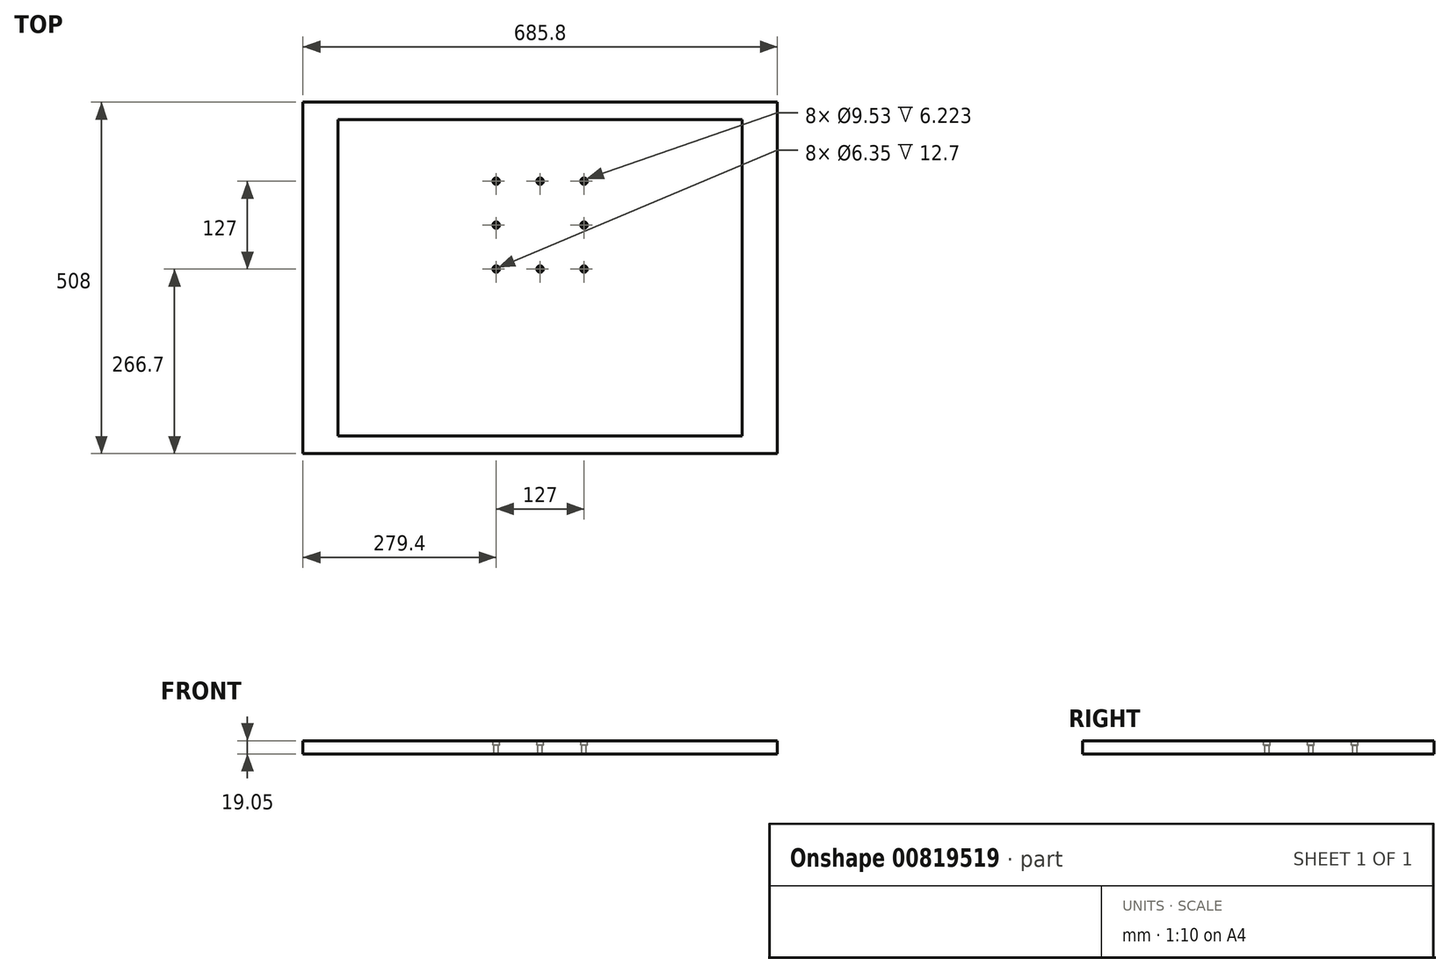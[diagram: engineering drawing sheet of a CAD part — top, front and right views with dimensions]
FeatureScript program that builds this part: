
annotation { "Feature Type Name" : "Feature", "Feature Type Description" : "" }
export const myFeature = defineFeature(function(context is Context, id is Id, definition is map)
    precondition{}
    {
        {
            var Q0;
            Q0=qCreatedBy(makeId("Top.planeOp"),FACE);
            var sketch = newSketch(context, id + "F0", { "sketchPlane" : qUnion([Q0])});
            skLineSegment(sketch, "E0.bottom", {"start": v(-292.1, 228.6) * mm, "end": v(292.1, 228.6) * mm, "construction": true});
            skLineSegment(sketch, "E0.top", {"start": v(-292.1, -228.6) * mm, "end": v(292.1, -228.6) * mm, "construction": true});
            skLineSegment(sketch, "E0.left", {"start": v(-292.1, 228.6) * mm, "end": v(-292.1, -228.6) * mm, "construction": true});
            skLineSegment(sketch, "E0.right", {"start": v(292.1, 228.6) * mm, "end": v(292.1, -228.6) * mm, "construction": true});
            skLineSegment(sketch, "E1.bottom", {"start": v(-342.9, 254) * mm, "end": v(342.9, 254) * mm});
            skLineSegment(sketch, "E1.top", {"start": v(-342.9, -254) * mm, "end": v(342.9, -254) * mm});
            skLineSegment(sketch, "E1.left", {"start": v(-342.9, 254) * mm, "end": v(-342.9, -254) * mm});
            skLineSegment(sketch, "E1.right", {"start": v(342.9, 254) * mm, "end": v(342.9, -254) * mm});
            skLineSegment(sketch, "E2", {"start": v(-292.1, 228.6) * mm, "end": v(292.1, -228.6) * mm, "construction": true});
            skLineSegment(sketch, "E3", {"start": v(292.1, 228.6) * mm, "end": v(-292.1, -228.6) * mm, "construction": true});
            skLineSegment(sketch, "E4", {"start": v(292.1, 0) * mm, "end": v(342.9, 0) * mm, "construction": true});
            skPoint(sketch, "E4.endSnap0", {"position": v(342.9, 0) * mm});
            skLineSegment(sketch, "E5", {"start": v(-292.1, 0) * mm, "end": v(-342.9, 0) * mm, "construction": true});
            skSolve(sketch);
        }
        {
            var Q0;
            Q0=qSketchRegion(id+"F0",true);
            extrude(context, id + "F1", {"entities" : qUnion([Q0]), "depth" : 19.05 * mm, "offsetDistance" : 25.4 * mm});
        }
        {
            var Q0;
            Q0=makeQuery(id+"F1.opExtrude","CAP_FACE",FACE,{"disambiguationData":[OSD([sQuery(id+"F0.wireOp",EDGE,"E1.bottom"),sQuery(id+"F0.wireOp",EDGE,"E1.top"),sQuery(id+"F0.wireOp",EDGE,"E1.left"),sQuery(id+"F0.wireOp",EDGE,"E1.right")])],"isStart":false});
            var sketch = newSketch(context, id + "F2", { "sketchPlane" : qUnion([Q0])});
            skCircle(sketch, "E6", {"center": v(-63.5, 139.7) * mm, "radius": 3.18 * mm});
            skCircle(sketch, "E7", {"center": v(0, 139.7) * mm, "radius": 3.18 * mm});
            skCircle(sketch, "E8", {"center": v(63.5, 139.7) * mm, "radius": 3.18 * mm});
            skCircle(sketch, "E9", {"center": v(63.5, 76.2) * mm, "radius": 3.18 * mm});
            skCircle(sketch, "E10", {"center": v(63.5, 12.7) * mm, "radius": 3.18 * mm});
            skCircle(sketch, "E11", {"center": v(0, 12.7) * mm, "radius": 3.18 * mm});
            skCircle(sketch, "E12", {"center": v(-63.5, 12.7) * mm, "radius": 3.18 * mm});
            skCircle(sketch, "E13", {"center": v(-63.5, 76.2) * mm, "radius": 3.18 * mm});
            skLineSegment(sketch, "E14", {"start": v(-63.5, 139.7) * mm, "end": v(0, 139.7) * mm, "construction": true});
            skLineSegment(sketch, "E15", {"start": v(63.5, 139.7) * mm, "end": v(0, 139.7) * mm, "construction": true});
            skLineSegment(sketch, "E16", {"start": v(-63.5, 139.7) * mm, "end": v(-63.5, 76.2) * mm, "construction": true});
            skLineSegment(sketch, "E17", {"start": v(-63.5, 76.2) * mm, "end": v(-63.5, 12.7) * mm, "construction": true});
            skSolve(sketch);
        }
        {
            var Q0;
            Q0=sQuery(id+"F2.wireOp",VERTEX,"E14.start");
            var Q1;
            Q1=sQuery(id+"F2.wireOp",VERTEX,"E16.end");
            var Q2;
            Q2=sQuery(id+"F2.wireOp",VERTEX,"E17.end");
            var Q3;
            Q3=sQuery(id+"F2.wireOp",VERTEX,"E11.center");
            var Q4;
            Q4=sQuery(id+"F2.wireOp",VERTEX,"E10.center");
            var Q5;
            Q5=sQuery(id+"F2.wireOp",VERTEX,"E9.center");
            var Q6;
            Q6=sQuery(id+"F2.wireOp",VERTEX,"E15.start");
            var Q7;
            Q7=sQuery(id+"F2.wireOp",VERTEX,"E14.end");
            var Q8;
            Q8=makeQuery(id+"F1.opExtrude","SWEPT_BODY",BODY,{"disambiguationData":[OSD([sQuery(id+"F0.wireOp",EDGE,"E1.bottom"),sQuery(id+"F0.wireOp",EDGE,"E1.top"),sQuery(id+"F0.wireOp",EDGE,"E1.left"),sQuery(id+"F0.wireOp",EDGE,"E1.right")])]});
            hole(context, id + "F3", {"style" : HoleStyle.C_BORE, "endStyle" : HoleEndStyle.THROUGH, "holeDiameter" : 6.35 * mm, "cBoreDiameter" : 9.52 * mm, "cBoreDepth" : 6.35 * mm, "majorDiameter" : 6.35 * mm, "isTappedThrough" : true, "tappedDepth" : 12.7 * mm, "tapClearance" : 3, "locations" : qUnion([Q0, Q1, Q2, Q3, Q4, Q5, Q6, Q7]), "scope" : qUnion([Q8])});
        }
        {
            var Q0;
            Q0=makeQuery(id+"F1.opExtrude","CAP_FACE",FACE,{"disambiguationData":[OSD([sQuery(id+"F0.wireOp",EDGE,"E1.bottom"),sQuery(id+"F0.wireOp",EDGE,"E1.top"),sQuery(id+"F0.wireOp",EDGE,"E1.left"),sQuery(id+"F0.wireOp",EDGE,"E1.right")])],"isStart":false});
            var sketch = newSketch(context, id + "F4", { "sketchPlane" : qUnion([Q0])});
            skLineSegment(sketch, "E18.bottom", {"start": v(-292.1, 228.6) * mm, "end": v(292.1, 228.6) * mm});
            skLineSegment(sketch, "E18.top", {"start": v(-292.1, -228.6) * mm, "end": v(292.1, -228.6) * mm});
            skLineSegment(sketch, "E18.left", {"start": v(-292.1, 228.6) * mm, "end": v(-292.1, -228.6) * mm});
            skLineSegment(sketch, "E18.right", {"start": v(292.1, 228.6) * mm, "end": v(292.1, -228.6) * mm});
            skLineSegment(sketch, "E19", {"start": v(-292.1, 228.6) * mm, "end": v(292.1, -228.6) * mm, "construction": true});
            skLineSegment(sketch, "E20", {"start": v(292.1, 228.6) * mm, "end": v(-292.1, -228.6) * mm, "construction": true});
            skSolve(sketch);
        }
        {
            var Q0;
            Q0 = qSketchRegion(id + "F4", true);
            extrude(context, id + "F5", {"entities" : qUnion([Q0]), "operationType" : NewBodyOperationType.REMOVE, "oppositeDirection" : true, "depth" : 0.13 * mm, "offsetDistance" : 25.4 * mm});
        }
    });
